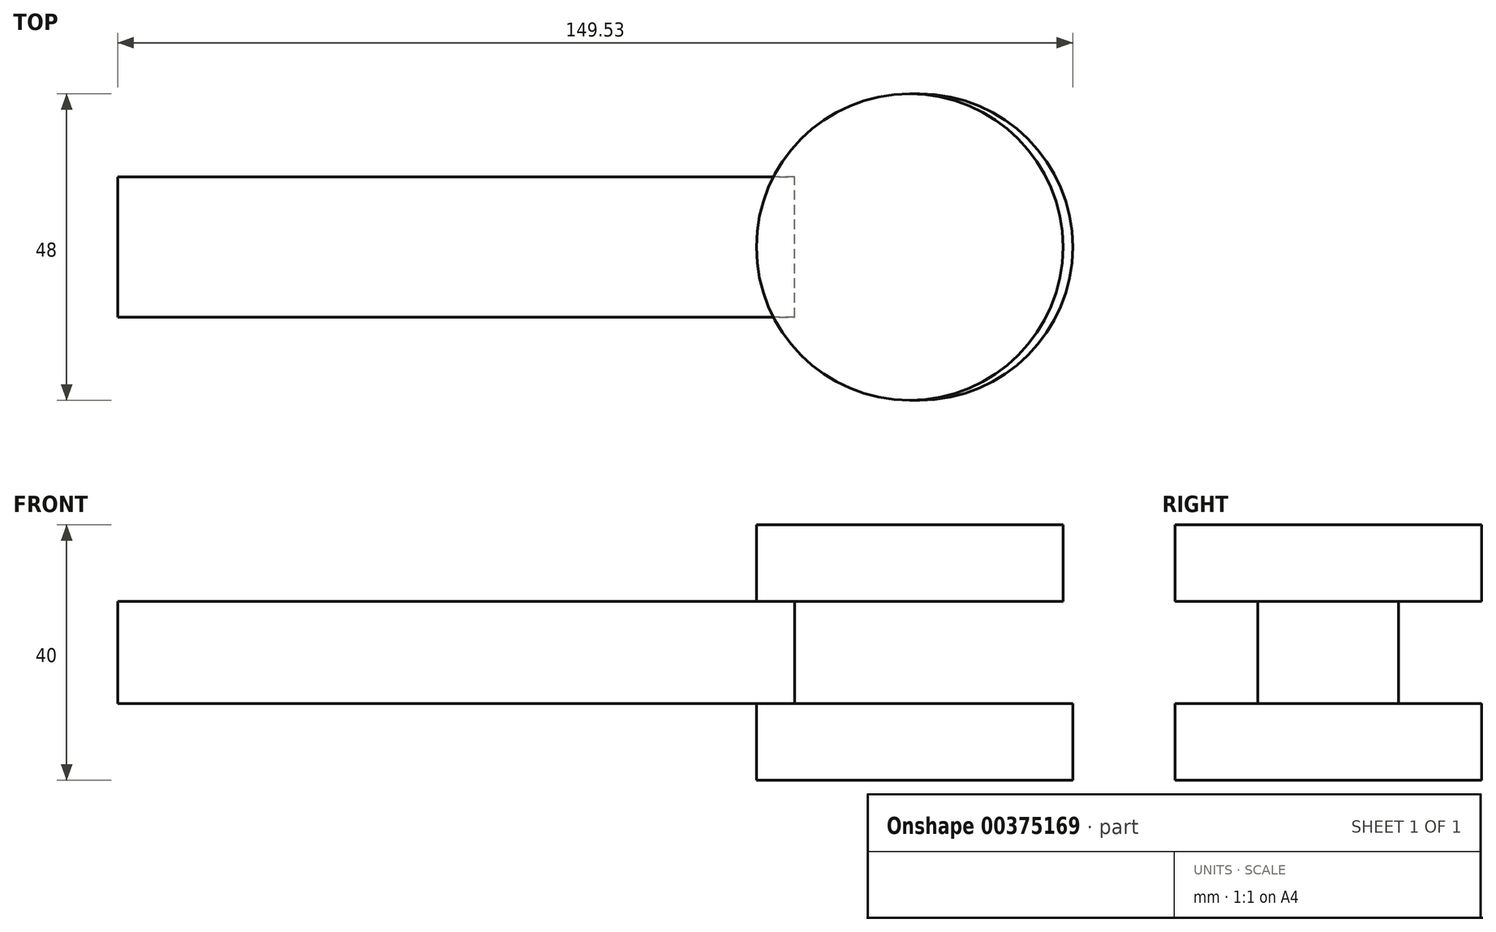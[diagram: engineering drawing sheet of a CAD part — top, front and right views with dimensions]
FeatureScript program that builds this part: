
annotation { "Feature Type Name" : "Feature", "Feature Type Description" : "" }
export const myFeature = defineFeature(function(context is Context, id is Id, definition is map)
    precondition{}
    {
        {
            var Q0;
            Q0=qCreatedBy(makeId("Front.planeOp"),FACE);
            var sketch = newSketch(context, id + "F0", { "sketchPlane" : qUnion([Q0])});
            skLineSegment(sketch, "E0", {"start": v(-71.99, 8.51) * mm, "end": v(-71.99, -7.49) * mm});
            skLineSegment(sketch, "E1", {"start": v(-71.99, -7.49) * mm, "end": v(28.01, -7.49) * mm});
            skLineSegment(sketch, "E2", {"start": v(-71.99, 8.51) * mm, "end": v(28.01, 8.51) * mm});
            skLineSegment(sketch, "E3", {"start": v(28.01, 8.51) * mm, "end": v(28.01, 20.51) * mm});
            skLineSegment(sketch, "E4", {"start": v(28.01, 20.51) * mm, "end": v(76.01, 20.51) * mm});
            skLineSegment(sketch, "E5", {"start": v(76.01, 20.51) * mm, "end": v(76.01, 8.51) * mm});
            skLineSegment(sketch, "E6", {"start": v(76.01, 8.51) * mm, "end": v(28.01, 8.51) * mm});
            skLineSegment(sketch, "E7", {"start": v(28.01, -7.49) * mm, "end": v(28.01, -19.49) * mm});
            skLineSegment(sketch, "E8", {"start": v(28.01, -19.49) * mm, "end": v(77.54, -19.49) * mm});
            skLineSegment(sketch, "E9", {"start": v(77.54, -19.49) * mm, "end": v(77.54, -7.49) * mm});
            skLineSegment(sketch, "E10", {"start": v(77.54, -7.49) * mm, "end": v(28.01, -7.49) * mm});
            skLineSegment(sketch, "E11", {"start": v(28.01, -7.49) * mm, "end": v(34.01, -7.49) * mm});
            skLineSegment(sketch, "E12", {"start": v(34.01, -7.49) * mm, "end": v(34.01, 8.51) * mm});
            skSolve(sketch);
        }
        {
            var Q0;
            {var subQ3=sQuery(id+"F0.wireOp",EDGE,"E3");Q0=makeQuery(id+"F0.imprint","IMPRINT",FACE,{"disambiguationData":[TD([[makeQuery(id+"F0.imprint","IMPRINT",EDGE,{"derivedFrom":subQ3}),-1.0]])]});}
            var Q1;
            Q1=makeQuery(id+"F0.imprint","IMPRINT",FACE,{"disambiguationData":[TD([[makeQuery(id+"F0.imprint","IMPRINT",EDGE,{"derivedFrom":sQuery(id+"F0.wireOp",EDGE,"E7")}),1.0]])]});
            extrude(context, id + "F1", {"entities" : qUnion([Q0, Q1]), "endBound" : BoundingType.SYMMETRIC, "depth" : 48 * mm});
        }
        {
            var Q0;
            Q0=makeQuery(id+"F0.imprint","IMPRINT",FACE,{"disambiguationData":[TD([[makeQuery(id+"F0.imprint","IMPRINT",EDGE,{"derivedFrom":sQuery(id+"F0.wireOp",EDGE,"E0")}),1.0]])]});
            extrude(context, id + "F2", {"entities" : qUnion([Q0]), "endBound" : BoundingType.SYMMETRIC, "depth" : 22 * mm});
        }
        {
            var Q0;
            Q0=makeQuery(id+"F1.opExtrude","CAP_EDGE",EDGE,{"disambiguationData":[OSD([sQuery(id+"F0.wireOp",EDGE,"E5")])],"isStart":false});
            var Q1;
            Q1=makeQuery(id+"F1.opExtrude","CAP_EDGE",EDGE,{"disambiguationData":[OSD([sQuery(id+"F0.wireOp",EDGE,"E5")])],"isStart":true});
            var Q2;
            Q2=makeQuery(id+"F1.opExtrude","CAP_EDGE",EDGE,{"disambiguationData":[OSD([sQuery(id+"F0.wireOp",EDGE,"E3")])],"isStart":false});
            var Q3;
            Q3=makeQuery(id+"F1.opExtrude","CAP_EDGE",EDGE,{"disambiguationData":[OSD([sQuery(id+"F0.wireOp",EDGE,"E3")])],"isStart":true});
            var Q4;
            Q4=makeQuery(id+"F1.opExtrude","CAP_EDGE",EDGE,{"disambiguationData":[OSD([sQuery(id+"F0.wireOp",EDGE,"E9")])],"isStart":true});
            var Q5;
            Q5=makeQuery(id+"F1.opExtrude","CAP_EDGE",EDGE,{"disambiguationData":[OSD([sQuery(id+"F0.wireOp",EDGE,"E9")])],"isStart":false});
            var Q6;
            Q6=makeQuery(id+"F1.opExtrude","CAP_EDGE",EDGE,{"disambiguationData":[OSD([sQuery(id+"F0.wireOp",EDGE,"E7")])],"isStart":false});
            var Q7;
            Q7=makeQuery(id+"F1.opExtrude","CAP_EDGE",EDGE,{"disambiguationData":[OSD([sQuery(id+"F0.wireOp",EDGE,"E7")])],"isStart":true});
            fillet(context, id + "F3", {"entities" : qUnion([Q0, Q1, Q2, Q3, Q4, Q5, Q6, Q7]), "radius" : 24 * mm, "tangentPropagation" : true, "allowEdgeOverflow" : false});
        }
    });
